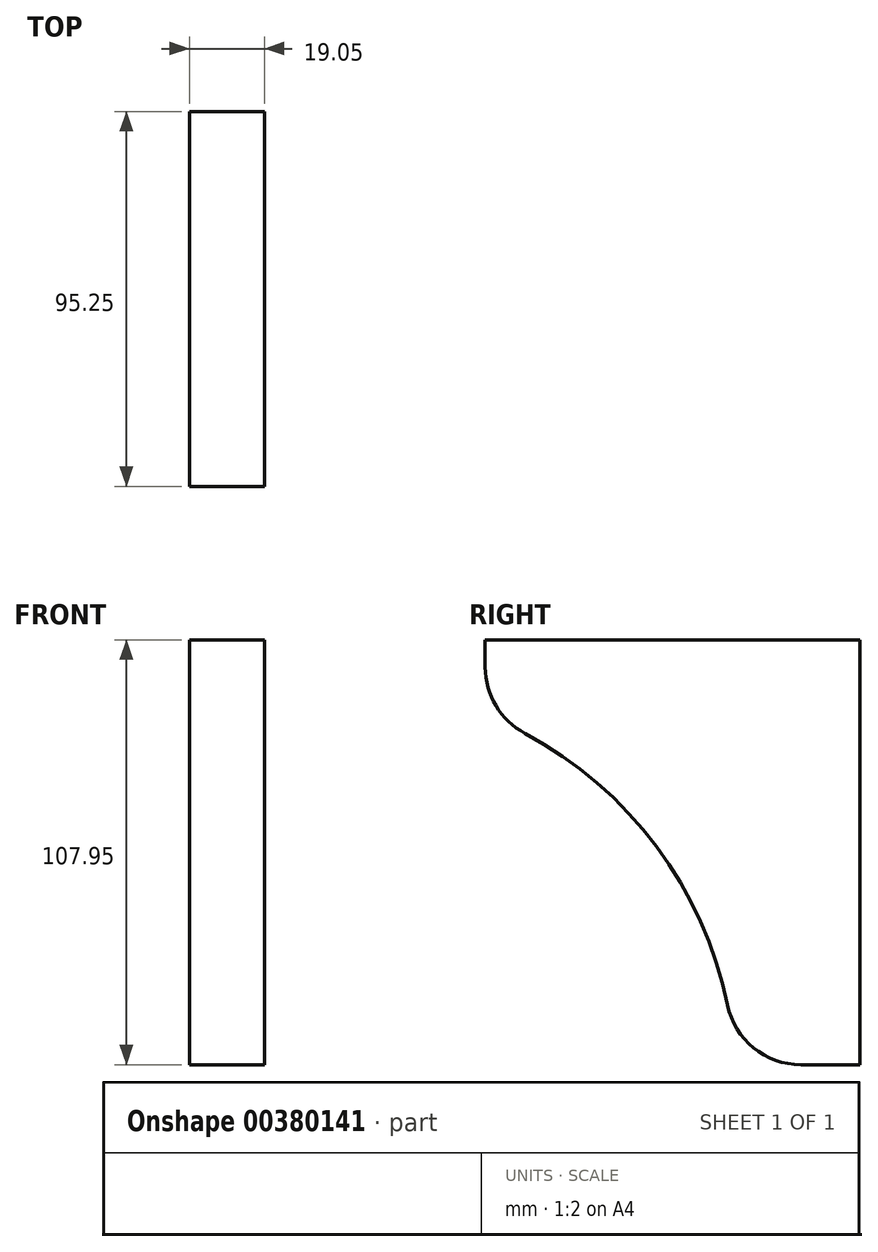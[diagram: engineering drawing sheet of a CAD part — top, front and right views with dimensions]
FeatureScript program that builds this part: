
annotation { "Feature Type Name" : "Feature", "Feature Type Description" : "" }
export const myFeature = defineFeature(function(context is Context, id is Id, definition is map)
    precondition{}
    {
        {
            var Q0;
            Q0=qCreatedBy(makeId("Right.planeOp"),FACE);
            var sketch = newSketch(context, id + "F0", { "sketchPlane" : qUnion([Q0])});
            skLineSegment(sketch, "E0", {"start": v(0, 0) * mm, "end": v(0, -107.95) * mm});
            skLineSegment(sketch, "E1", {"start": v(0, -107.95) * mm, "end": v(-31.75, -107.95) * mm});
            skLineSegment(sketch, "E2", {"start": v(0, 0) * mm, "end": v(-95.25, 0) * mm});
            skLineSegment(sketch, "E3", {"start": v(-95.25, 0) * mm, "end": v(-95.25, -19.05) * mm});
            skArc(sketch, "E4", {"start": v(-31.75, -107.95) * mm, "mid": v(-50.53, -54.24) * mm, "end": v(-95.25, -19.05) * mm});
            skSolve(sketch);
        }
        {
            var Q0;
            Q0 = qSketchRegion(id + "F0", true);
            extrude(context, id + "F1", {"entities" : qUnion([Q0]), "depth" : 19.05 * mm});
        }
        {
            var Q0;
            Q0=makeQuery(id+"F1.opExtrude","SWEPT_EDGE",EDGE,{"disambiguationData":[OSD([sQuery(id+"F0.wireOp",EDGE,"E3"),sQuery(id+"F0.wireOp",EDGE,"E4")])]});
            var Q1;
            Q1=makeQuery(id+"F1.opExtrude","SWEPT_EDGE",EDGE,{"disambiguationData":[OSD([sQuery(id+"F0.wireOp",EDGE,"E1"),sQuery(id+"F0.wireOp",EDGE,"E4")])]});
            fillet(context, id + "F2", {"entities" : qUnion([Q0, Q1]), "radius" : 19.05 * mm, "tangentPropagation" : true, "allowEdgeOverflow" : false});
        }
    });
